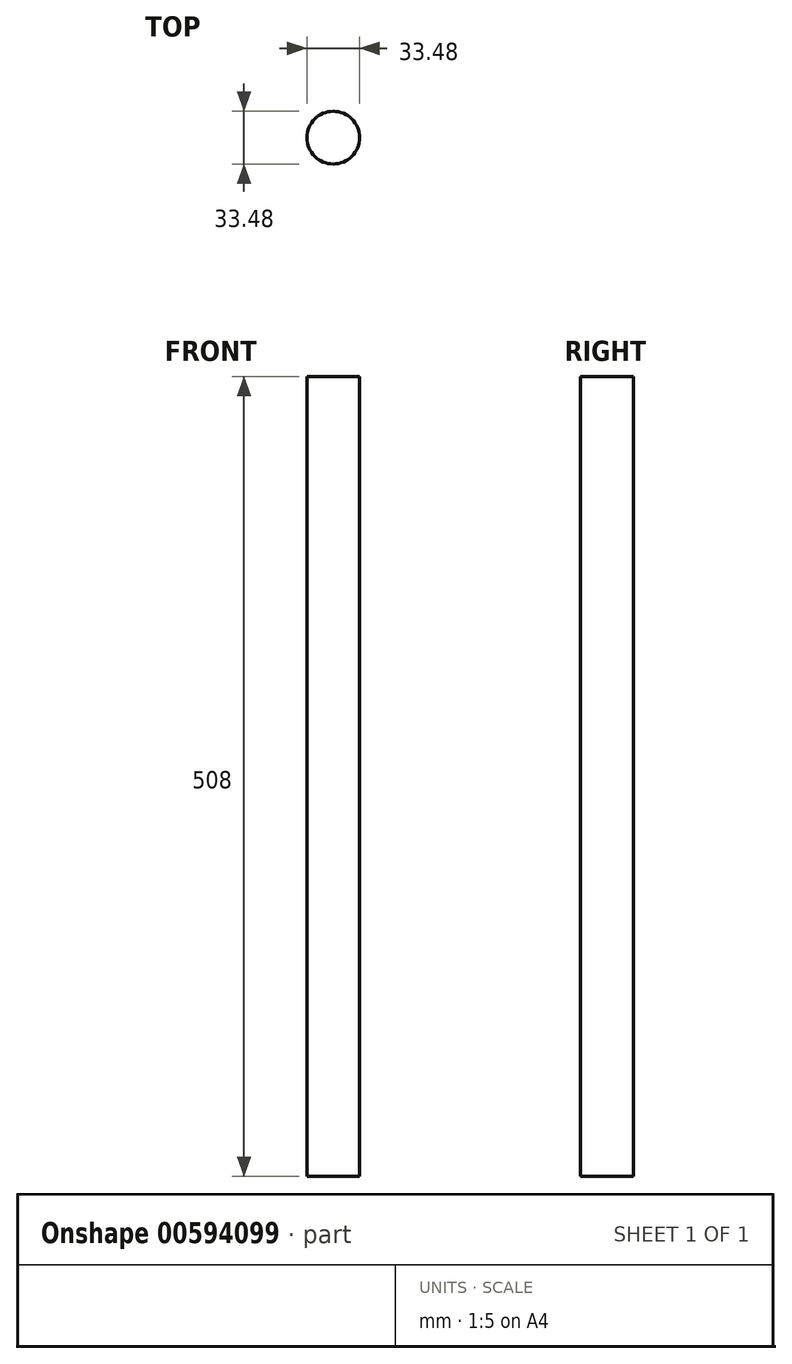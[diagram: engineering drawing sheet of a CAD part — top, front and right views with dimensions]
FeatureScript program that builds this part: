
annotation { "Feature Type Name" : "Feature", "Feature Type Description" : "" }
export const myFeature = defineFeature(function(context is Context, id is Id, definition is map)
    precondition{}
    {
        {
            var Q0;
            Q0=qCreatedBy(makeId("Top.planeOp"),FACE);
            var sketch = newSketch(context, id + "F0", { "sketchPlane" : qUnion([Q0])});
            skCircle(sketch, "E0", {"center": v(0, 0) * mm, "radius": 16.74 * mm});
            skSolve(sketch);
        }
        {
            var Q0;
            Q0=makeQuery(id+"F0.imprint","IMPRINT",FACE,{"disambiguationData":[TD([[makeQuery(id+"F0.imprint","IMPRINT",EDGE,{"derivedFrom":sQuery(id+"F0.wireOp",EDGE,"E0")}),1.0]])]});
            extrude(context, id + "F1", {"entities" : qUnion([Q0]), "depth" : 508 * mm, "offsetDistance" : 25.4 * mm});
        }
    });
